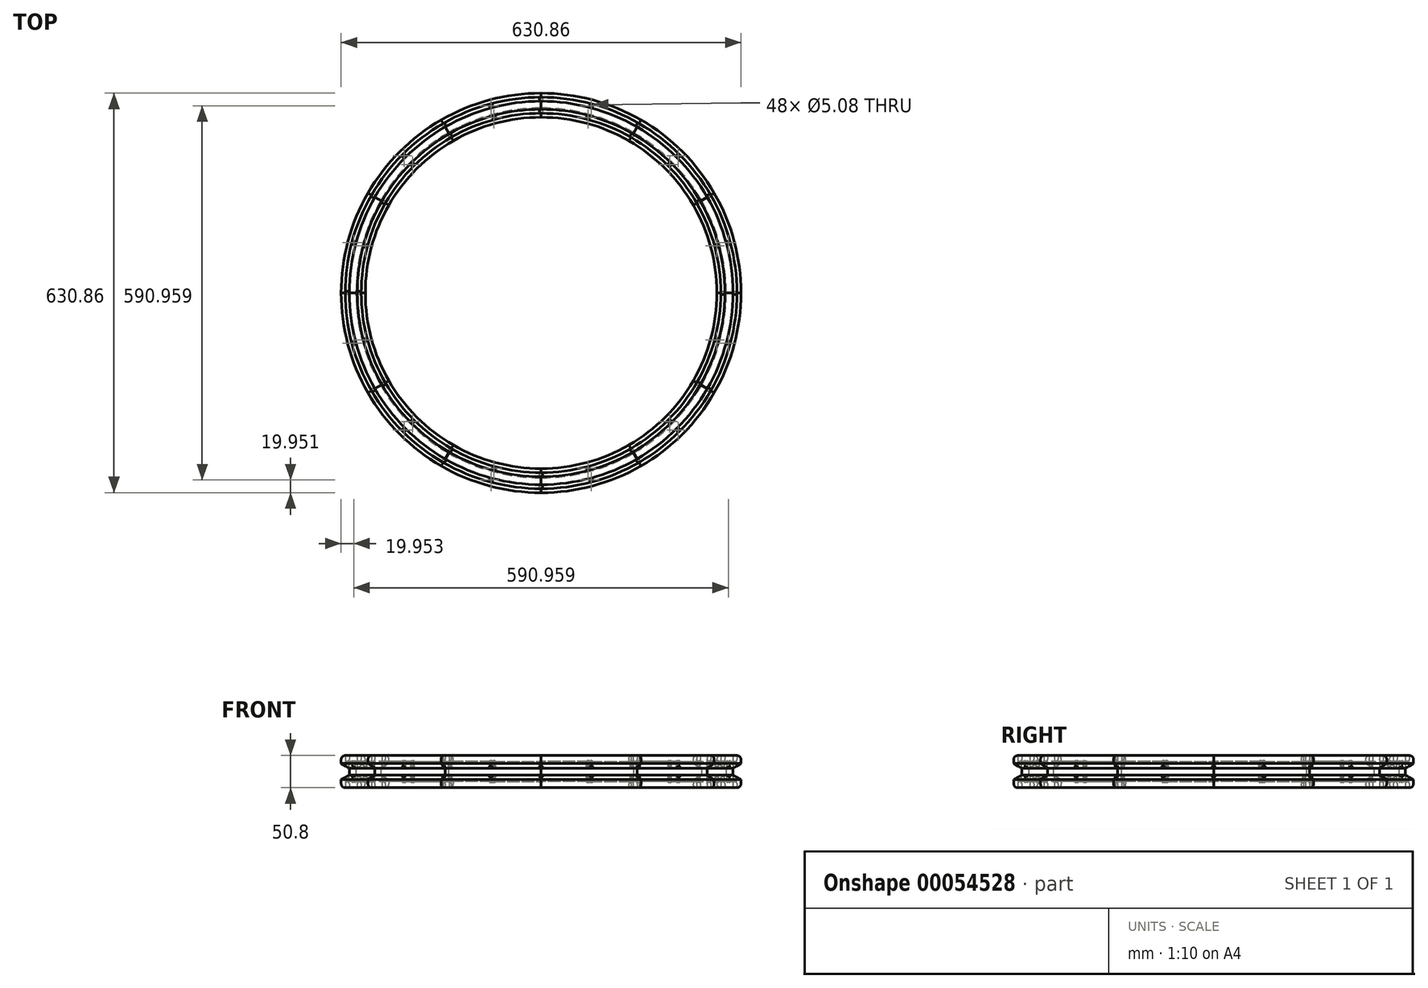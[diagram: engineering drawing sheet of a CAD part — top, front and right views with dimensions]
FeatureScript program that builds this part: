
annotation { "Feature Type Name" : "Feature", "Feature Type Description" : "" }
export const myFeature = defineFeature(function(context is Context, id is Id, definition is map)
    precondition{}
    {
        {
            var Q0;
            Q0=qCreatedBy(makeId("Front.planeOp"),FACE);
            var sketch = newSketch(context, id + "F0", { "sketchPlane" : qUnion([Q0])});
            skLineSegment(sketch, "E0", {"start": v(-51.22, 16.91) * mm, "end": v(-51.22, 6.28) * mm});
            skPoint(sketch, "E1.visualSharp", {"position": v(-4.7, -13.74) * mm});
            skArc(sketch, "E1.filletArc", {"start": v(-42.8, -13.8) * mm, "mid": v(-38.3, -11.94) * mm, "end": v(-36.45, -7.45) * mm});
            skPoint(sketch, "E2.visualSharp", {"position": v(-4.7, 37.06) * mm});
            skArc(sketch, "E2.filletArc", {"start": v(-36.45, 30.65) * mm, "mid": v(-38.3, 35.14) * mm, "end": v(-42.8, 37) * mm});
            skPoint(sketch, "E3", {"position": v(240.88, 11.6) * mm});
            skLineSegment(sketch, "E4", {"start": v(240.88, 11.6) * mm, "end": v(240.88, 0) * mm});
            skLineSegment(sketch, "E5", {"start": v(-36.45, 24.3) * mm, "end": v(-51.22, 16.91) * mm});
            skLineSegment(sketch, "E6", {"start": v(-36.45, 24.3) * mm, "end": v(-36.45, 30.65) * mm});
            skLineSegment(sketch, "E7", {"start": v(-36.45, -1.1) * mm, "end": v(-51.22, 6.28) * mm});
            skLineSegment(sketch, "E8", {"start": v(-36.45, -1.1) * mm, "end": v(-36.45, -7.45) * mm});
            skLineSegment(sketch, "E9", {"start": v(-51.22, 16.91) * mm, "end": v(-51.22, 11.6) * mm});
            skLineSegment(sketch, "E10", {"start": v(-42.8, 303.76) * mm, "end": v(-52.22, 303.76) * mm});
            skPoint(sketch, "E11", {"position": v(-45.97, 30.7) * mm});
            skPoint(sketch, "E12", {"position": v(-45.97, -7.45) * mm});
            skPoint(sketch, "E13", {"position": v(-45.9, 27.47) * mm});
            skPoint(sketch, "E14", {"position": v(-49.15, 30.65) * mm});
            skPoint(sketch, "E15", {"position": v(-49.15, -7.45) * mm});
            skPoint(sketch, "E16", {"position": v(-45.97, -4.28) * mm});
            skArc(sketch, "E17", {"start": v(-42.8, -7.45) * mm, "mid": v(-45.97, -4.28) * mm, "end": v(-49.15, -7.45) * mm});
            skArc(sketch, "E18", {"start": v(-49.15, 30.65) * mm, "mid": v(-45.97, 27.47) * mm, "end": v(-42.8, 30.65) * mm});
            skLineSegment(sketch, "E19", {"start": v(-49.15, 37) * mm, "end": v(-49.15, 30.65) * mm});
            skLineSegment(sketch, "E20", {"start": v(-42.8, 37) * mm, "end": v(-42.8, 30.65) * mm});
            skLineSegment(sketch, "E21", {"start": v(-49.15, -7.45) * mm, "end": v(-49.15, -13.8) * mm});
            skLineSegment(sketch, "E22", {"start": v(-42.8, -7.45) * mm, "end": v(-42.8, -13.8) * mm});
            skLineSegment(sketch, "E23", {"start": v(-49.15, 37) * mm, "end": v(-61.85, 37) * mm});
            skLineSegment(sketch, "E24", {"start": v(-49.15, -13.8) * mm, "end": v(-61.85, -13.8) * mm});
            skLineSegment(sketch, "E25", {"start": v(-36.45, 16.91) * mm, "end": v(-36.45, 24.3) * mm, "construction": true});
            skLineSegment(sketch, "E26", {"start": v(-36.45, 16.91) * mm, "end": v(-51.22, 16.91) * mm, "construction": true});
            skLineSegment(sketch, "E27", {"start": v(-36.45, 6.28) * mm, "end": v(-36.45, -1.1) * mm, "construction": true});
            skLineSegment(sketch, "E28", {"start": v(-36.45, 6.28) * mm, "end": v(-51.22, 6.28) * mm, "construction": true});
            skPoint(sketch, "E29", {"position": v(-61.85, -7.45) * mm});
            skLineSegment(sketch, "E30", {"start": v(-61.85, -13.8) * mm, "end": v(-68.2, -13.8) * mm, "construction": true});
            skLineSegment(sketch, "E31", {"start": v(-68.2, -7.45) * mm, "end": v(-68.2, -13.8) * mm});
            skPoint(sketch, "E32", {"position": v(-65.02, -4.28) * mm});
            skPoint(sketch, "E32.positionSnap0", {"position": v(-65.02, -13.8) * mm});
            skArc(sketch, "E33", {"start": v(-61.85, -7.45) * mm, "mid": v(-65.02, -4.28) * mm, "end": v(-68.2, -7.45) * mm});
            skLineSegment(sketch, "E34", {"start": v(-68.2, -13.8) * mm, "end": v(-68.2, -13.8) * mm});
            skLineSegment(sketch, "E35", {"start": v(-74.55, -7.45) * mm, "end": v(-74.55, -7.45) * mm});
            skPoint(sketch, "E36.visualSharp", {"position": v(-74.55, -13.8) * mm});
            skArc(sketch, "E36.filletArc", {"start": v(-74.55, -7.45) * mm, "mid": v(-72.69, -11.94) * mm, "end": v(-68.2, -13.8) * mm});
            skLineSegment(sketch, "E37", {"start": v(-74.55, 30.65) * mm, "end": v(-74.55, -7.45) * mm, "construction": true});
            skLineSegment(sketch, "E38", {"start": v(-74.55, -7.45) * mm, "end": v(-74.55, -1.1) * mm});
            skLineSegment(sketch, "E39", {"start": v(-74.55, -1.1) * mm, "end": v(-61.85, 6.28) * mm});
            skLineSegment(sketch, "E40", {"start": v(-61.85, 16.91) * mm, "end": v(-74.55, 24.3) * mm});
            skLineSegment(sketch, "E41", {"start": v(-61.85, -7.45) * mm, "end": v(-61.85, -13.8) * mm});
            skLineSegment(sketch, "E42", {"start": v(-61.85, 6.28) * mm, "end": v(-61.85, 16.91) * mm});
            skLineSegment(sketch, "E43", {"start": v(-74.55, 24.3) * mm, "end": v(-74.55, 30.65) * mm});
            skLineSegment(sketch, "E44", {"start": v(-74.55, 30.65) * mm, "end": v(-74.55, 30.65) * mm});
            skLineSegment(sketch, "E45", {"start": v(-68.2, 37) * mm, "end": v(-68.2, 37) * mm});
            skPoint(sketch, "E45.endSnap0", {"position": v(-68.2, 20.6) * mm});
            skLineSegment(sketch, "E46", {"start": v(-68.2, 37) * mm, "end": v(-61.85, 37) * mm, "construction": true});
            skPoint(sketch, "E47.visualSharp", {"position": v(-74.55, 37) * mm});
            skArc(sketch, "E47.filletArc", {"start": v(-68.2, 37) * mm, "mid": v(-72.69, 35.14) * mm, "end": v(-74.55, 30.65) * mm});
            skLineSegment(sketch, "E48", {"start": v(-68.2, 37) * mm, "end": v(-68.2, 30.65) * mm});
            skLineSegment(sketch, "E49", {"start": v(-61.85, 37) * mm, "end": v(-61.85, 30.65) * mm});
            skPoint(sketch, "E50", {"position": v(-65.02, 27.47) * mm});
            skArc(sketch, "E51", {"start": v(-68.2, 30.65) * mm, "mid": v(-65.02, 27.47) * mm, "end": v(-61.85, 30.65) * mm});
            skSolve(sketch);
        }
        {
            var Q0;
            Q0=makeQuery(id+"F0.imprint","IMPRINT",FACE,{"disambiguationData":[TD([[makeQuery(id+"F0.imprint","IMPRINT",EDGE,{"derivedFrom":sQuery(id+"F0.wireOp",EDGE,"E0")}),-1.0]])]});
            var Q1;
            Q1=sQuery(id+"F0.wireOp",EDGE,"E4");
            revolve(context, id + "F1", {"entities" : qUnion([Q0]), "axis" : qUnion([Q1]), "revolveType" : RevolveType.ONE_DIRECTION, "angle" : 30 * degree});
        }
        {
            var Q0;
            Q0=makeQuery(id+"F1.opRevolve","SWEPT_FACE",FACE,{"disambiguationData":[OSD([sQuery(id+"F0.wireOp",EDGE,"E23")])]});
            var sketch = newSketch(context, id + "F2", { "sketchPlane" : qUnion([Q0])});
            skPoint(sketch, "E52", {"position": v(-61.85, 0) * mm});
            skPoint(sketch, "E53", {"position": v(-49.15, 0) * mm});
            skLineSegment(sketch, "E54", {"start": v(-61.85, 0) * mm, "end": v(-68.2, 0) * mm});
            skPoint(sketch, "E55", {"position": v(-65.02, 0) * mm});
            skPoint(sketch, "E56", {"position": v(-68.2, 0) * mm});
            skPoint(sketch, "E57", {"position": v(-21.29, 151.36) * mm});
            skLineSegment(sketch, "E58", {"start": v(-21.29, 151.36) * mm, "end": v(-26.79, 154.54) * mm});
            skPoint(sketch, "E59", {"position": v(-24.04, 152.95) * mm});
            skPoint(sketch, "E60", {"position": v(-51.53, 78.35) * mm});
            skArc(sketch, "E61", {"start": v(-68.2, 0) * mm, "mid": v(-57.66, 80) * mm, "end": v(-26.79, 154.54) * mm});
            skPoint(sketch, "E62", {"position": v(-57.66, 80) * mm});
            skLineSegment(sketch, "E63", {"start": v(-51.53, 78.35) * mm, "end": v(-57.66, 80) * mm});
            skPoint(sketch, "E64", {"position": v(-54.6, 79.17) * mm});
            skPoint(sketch, "E65", {"position": v(-10.29, 145.01) * mm});
            skPoint(sketch, "E66", {"position": v(-39.26, 75.06) * mm});
            skArc(sketch, "E67", {"start": v(-49.15, 0) * mm, "mid": v(-39.26, 75.06) * mm, "end": v(-10.29, 145.01) * mm});
            skLineSegment(sketch, "E68", {"start": v(-49.15, 0) * mm, "end": v(-42.8, 0) * mm});
            skPoint(sketch, "E69", {"position": v(-42.8, 0) * mm});
            skLineSegment(sketch, "E70", {"start": v(-10.29, 145.01) * mm, "end": v(-4.79, 141.84) * mm});
            skPoint(sketch, "E71", {"position": v(-4.79, 141.84) * mm});
            skArc(sketch, "E72", {"start": v(-42.8, 0) * mm, "mid": v(-33.13, 73.42) * mm, "end": v(-4.79, 141.84) * mm});
            skPoint(sketch, "E73", {"position": v(-33.13, 73.42) * mm});
            skLineSegment(sketch, "E74", {"start": v(-39.26, 75.06) * mm, "end": v(-33.13, 73.42) * mm});
            skPoint(sketch, "E75", {"position": v(-36.2, 73.42) * mm});
            skPoint(sketch, "E75.positionSnap0", {"position": v(-36.2, 74.24) * mm});
            skPoint(sketch, "E76", {"position": v(-45.97, 0) * mm});
            skPoint(sketch, "E77", {"position": v(-7.54, 143.43) * mm});
            skSolve(sketch);
        }
        {
            var Q0;
            Q0=sQuery(id+"F2.wireOp",VERTEX,"E64");
            var Q1;
            Q1=makeQuery(id+"F1.opRevolve","SWEPT_BODY",BODY,{"disambiguationData":[OSD([sQuery(id+"F0.wireOp",EDGE,"E0"),sQuery(id+"F0.wireOp",EDGE,"E1.filletArc"),sQuery(id+"F0.wireOp",EDGE,"E2.filletArc"),sQuery(id+"F0.wireOp",EDGE,"E5"),sQuery(id+"F0.wireOp",EDGE,"E6"),sQuery(id+"F0.wireOp",EDGE,"E7"),sQuery(id+"F0.wireOp",EDGE,"E8"),sQuery(id+"F0.wireOp",EDGE,"E9"),sQuery(id+"F0.wireOp",EDGE,"E17"),sQuery(id+"F0.wireOp",EDGE,"E18"),sQuery(id+"F0.wireOp",EDGE,"E19"),sQuery(id+"F0.wireOp",EDGE,"E20"),sQuery(id+"F0.wireOp",EDGE,"E21"),sQuery(id+"F0.wireOp",EDGE,"E22"),sQuery(id+"F0.wireOp",EDGE,"E23"),sQuery(id+"F0.wireOp",EDGE,"E24"),sQuery(id+"F0.wireOp",EDGE,"E31"),sQuery(id+"F0.wireOp",EDGE,"E33"),sQuery(id+"F0.wireOp",EDGE,"E36.filletArc"),sQuery(id+"F0.wireOp",EDGE,"E38"),sQuery(id+"F0.wireOp",EDGE,"E39"),sQuery(id+"F0.wireOp",EDGE,"E40"),sQuery(id+"F0.wireOp",EDGE,"E41"),sQuery(id+"F0.wireOp",EDGE,"E42"),sQuery(id+"F0.wireOp",EDGE,"E43"),sQuery(id+"F0.wireOp",EDGE,"E47.filletArc"),sQuery(id+"F0.wireOp",EDGE,"E48"),sQuery(id+"F0.wireOp",EDGE,"E49"),sQuery(id+"F0.wireOp",EDGE,"E51")])]});
            hole(context, id + "F3", {"style" : HoleStyle.SIMPLE, "endStyle" : HoleEndStyle.THROUGH, "holeDiameter" : 5.08 * mm, "locations" : qUnion([Q0]), "scope" : qUnion([Q1]), "isTappedThrough" : true});
        }
        {
            var Q0;
            Q0=sQuery(id+"F2.wireOp",VERTEX,"E55");
            var Q1;
            Q1=makeQuery(id+"F1.opRevolve","SWEPT_BODY",BODY,{"disambiguationData":[OSD([sQuery(id+"F0.wireOp",EDGE,"E0"),sQuery(id+"F0.wireOp",EDGE,"E1.filletArc"),sQuery(id+"F0.wireOp",EDGE,"E2.filletArc"),sQuery(id+"F0.wireOp",EDGE,"E5"),sQuery(id+"F0.wireOp",EDGE,"E6"),sQuery(id+"F0.wireOp",EDGE,"E7"),sQuery(id+"F0.wireOp",EDGE,"E8"),sQuery(id+"F0.wireOp",EDGE,"E9"),sQuery(id+"F0.wireOp",EDGE,"E17"),sQuery(id+"F0.wireOp",EDGE,"E18"),sQuery(id+"F0.wireOp",EDGE,"E19"),sQuery(id+"F0.wireOp",EDGE,"E20"),sQuery(id+"F0.wireOp",EDGE,"E21"),sQuery(id+"F0.wireOp",EDGE,"E22"),sQuery(id+"F0.wireOp",EDGE,"E23"),sQuery(id+"F0.wireOp",EDGE,"E24"),sQuery(id+"F0.wireOp",EDGE,"E31"),sQuery(id+"F0.wireOp",EDGE,"E33"),sQuery(id+"F0.wireOp",EDGE,"E36.filletArc"),sQuery(id+"F0.wireOp",EDGE,"E38"),sQuery(id+"F0.wireOp",EDGE,"E39"),sQuery(id+"F0.wireOp",EDGE,"E40"),sQuery(id+"F0.wireOp",EDGE,"E41"),sQuery(id+"F0.wireOp",EDGE,"E42"),sQuery(id+"F0.wireOp",EDGE,"E43"),sQuery(id+"F0.wireOp",EDGE,"E47.filletArc"),sQuery(id+"F0.wireOp",EDGE,"E48"),sQuery(id+"F0.wireOp",EDGE,"E49"),sQuery(id+"F0.wireOp",EDGE,"E51")])]});
            hole(context, id + "F4", {"style" : HoleStyle.SIMPLE, "endStyle" : HoleEndStyle.THROUGH, "holeDiameter" : 5.08 * mm, "locations" : qUnion([Q0]), "scope" : qUnion([Q1]), "isTappedThrough" : true});
        }
        {
            var Q0;
            Q0=sQuery(id+"F2.wireOp",VERTEX,"E59");
            var Q1;
            Q1=makeQuery(id+"F1.opRevolve","SWEPT_BODY",BODY,{"disambiguationData":[OSD([sQuery(id+"F0.wireOp",EDGE,"E0"),sQuery(id+"F0.wireOp",EDGE,"E1.filletArc"),sQuery(id+"F0.wireOp",EDGE,"E2.filletArc"),sQuery(id+"F0.wireOp",EDGE,"E5"),sQuery(id+"F0.wireOp",EDGE,"E6"),sQuery(id+"F0.wireOp",EDGE,"E7"),sQuery(id+"F0.wireOp",EDGE,"E8"),sQuery(id+"F0.wireOp",EDGE,"E9"),sQuery(id+"F0.wireOp",EDGE,"E17"),sQuery(id+"F0.wireOp",EDGE,"E18"),sQuery(id+"F0.wireOp",EDGE,"E19"),sQuery(id+"F0.wireOp",EDGE,"E20"),sQuery(id+"F0.wireOp",EDGE,"E21"),sQuery(id+"F0.wireOp",EDGE,"E22"),sQuery(id+"F0.wireOp",EDGE,"E23"),sQuery(id+"F0.wireOp",EDGE,"E24"),sQuery(id+"F0.wireOp",EDGE,"E31"),sQuery(id+"F0.wireOp",EDGE,"E33"),sQuery(id+"F0.wireOp",EDGE,"E36.filletArc"),sQuery(id+"F0.wireOp",EDGE,"E38"),sQuery(id+"F0.wireOp",EDGE,"E39"),sQuery(id+"F0.wireOp",EDGE,"E40"),sQuery(id+"F0.wireOp",EDGE,"E41"),sQuery(id+"F0.wireOp",EDGE,"E42"),sQuery(id+"F0.wireOp",EDGE,"E43"),sQuery(id+"F0.wireOp",EDGE,"E47.filletArc"),sQuery(id+"F0.wireOp",EDGE,"E48"),sQuery(id+"F0.wireOp",EDGE,"E49"),sQuery(id+"F0.wireOp",EDGE,"E51")])]});
            hole(context, id + "F5", {"style" : HoleStyle.SIMPLE, "endStyle" : HoleEndStyle.THROUGH, "holeDiameter" : 5.08 * mm, "locations" : qUnion([Q0]), "scope" : qUnion([Q1]), "isTappedThrough" : true});
        }
        {
            var Q0;
            Q0=sQuery(id+"F2.wireOp",VERTEX,"E76");
            var Q1;
            Q1=makeQuery(id+"F1.opRevolve","SWEPT_BODY",BODY,{"disambiguationData":[OSD([sQuery(id+"F0.wireOp",EDGE,"E0"),sQuery(id+"F0.wireOp",EDGE,"E1.filletArc"),sQuery(id+"F0.wireOp",EDGE,"E2.filletArc"),sQuery(id+"F0.wireOp",EDGE,"E5"),sQuery(id+"F0.wireOp",EDGE,"E6"),sQuery(id+"F0.wireOp",EDGE,"E7"),sQuery(id+"F0.wireOp",EDGE,"E8"),sQuery(id+"F0.wireOp",EDGE,"E9"),sQuery(id+"F0.wireOp",EDGE,"E17"),sQuery(id+"F0.wireOp",EDGE,"E18"),sQuery(id+"F0.wireOp",EDGE,"E19"),sQuery(id+"F0.wireOp",EDGE,"E20"),sQuery(id+"F0.wireOp",EDGE,"E21"),sQuery(id+"F0.wireOp",EDGE,"E22"),sQuery(id+"F0.wireOp",EDGE,"E23"),sQuery(id+"F0.wireOp",EDGE,"E24"),sQuery(id+"F0.wireOp",EDGE,"E31"),sQuery(id+"F0.wireOp",EDGE,"E33"),sQuery(id+"F0.wireOp",EDGE,"E36.filletArc"),sQuery(id+"F0.wireOp",EDGE,"E38"),sQuery(id+"F0.wireOp",EDGE,"E39"),sQuery(id+"F0.wireOp",EDGE,"E40"),sQuery(id+"F0.wireOp",EDGE,"E41"),sQuery(id+"F0.wireOp",EDGE,"E42"),sQuery(id+"F0.wireOp",EDGE,"E43"),sQuery(id+"F0.wireOp",EDGE,"E47.filletArc"),sQuery(id+"F0.wireOp",EDGE,"E48"),sQuery(id+"F0.wireOp",EDGE,"E49"),sQuery(id+"F0.wireOp",EDGE,"E51")])]});
            hole(context, id + "F6", {"style" : HoleStyle.SIMPLE, "endStyle" : HoleEndStyle.THROUGH, "holeDiameter" : 5.08 * mm, "locations" : qUnion([Q0]), "scope" : qUnion([Q1]), "isTappedThrough" : true});
        }
        {
            var Q0;
            Q0=sQuery(id+"F2.wireOp",VERTEX,"E75.positionSnap0");
            var Q1;
            Q1=makeQuery(id+"F1.opRevolve","SWEPT_BODY",BODY,{"disambiguationData":[OSD([sQuery(id+"F0.wireOp",EDGE,"E0"),sQuery(id+"F0.wireOp",EDGE,"E1.filletArc"),sQuery(id+"F0.wireOp",EDGE,"E2.filletArc"),sQuery(id+"F0.wireOp",EDGE,"E5"),sQuery(id+"F0.wireOp",EDGE,"E6"),sQuery(id+"F0.wireOp",EDGE,"E7"),sQuery(id+"F0.wireOp",EDGE,"E8"),sQuery(id+"F0.wireOp",EDGE,"E9"),sQuery(id+"F0.wireOp",EDGE,"E17"),sQuery(id+"F0.wireOp",EDGE,"E18"),sQuery(id+"F0.wireOp",EDGE,"E19"),sQuery(id+"F0.wireOp",EDGE,"E20"),sQuery(id+"F0.wireOp",EDGE,"E21"),sQuery(id+"F0.wireOp",EDGE,"E22"),sQuery(id+"F0.wireOp",EDGE,"E23"),sQuery(id+"F0.wireOp",EDGE,"E24"),sQuery(id+"F0.wireOp",EDGE,"E31"),sQuery(id+"F0.wireOp",EDGE,"E33"),sQuery(id+"F0.wireOp",EDGE,"E36.filletArc"),sQuery(id+"F0.wireOp",EDGE,"E38"),sQuery(id+"F0.wireOp",EDGE,"E39"),sQuery(id+"F0.wireOp",EDGE,"E40"),sQuery(id+"F0.wireOp",EDGE,"E41"),sQuery(id+"F0.wireOp",EDGE,"E42"),sQuery(id+"F0.wireOp",EDGE,"E43"),sQuery(id+"F0.wireOp",EDGE,"E47.filletArc"),sQuery(id+"F0.wireOp",EDGE,"E48"),sQuery(id+"F0.wireOp",EDGE,"E49"),sQuery(id+"F0.wireOp",EDGE,"E51")])]});
            hole(context, id + "F7", {"style" : HoleStyle.SIMPLE, "endStyle" : HoleEndStyle.THROUGH, "holeDiameter" : 5.08 * mm, "locations" : qUnion([Q0]), "scope" : qUnion([Q1]), "isTappedThrough" : true});
        }
        {
            var Q0;
            Q0=sQuery(id+"F2.wireOp",VERTEX,"E77");
            var Q1;
            Q1=makeQuery(id+"F1.opRevolve","SWEPT_BODY",BODY,{"disambiguationData":[OSD([sQuery(id+"F0.wireOp",EDGE,"E0"),sQuery(id+"F0.wireOp",EDGE,"E1.filletArc"),sQuery(id+"F0.wireOp",EDGE,"E2.filletArc"),sQuery(id+"F0.wireOp",EDGE,"E5"),sQuery(id+"F0.wireOp",EDGE,"E6"),sQuery(id+"F0.wireOp",EDGE,"E7"),sQuery(id+"F0.wireOp",EDGE,"E8"),sQuery(id+"F0.wireOp",EDGE,"E9"),sQuery(id+"F0.wireOp",EDGE,"E17"),sQuery(id+"F0.wireOp",EDGE,"E18"),sQuery(id+"F0.wireOp",EDGE,"E19"),sQuery(id+"F0.wireOp",EDGE,"E20"),sQuery(id+"F0.wireOp",EDGE,"E21"),sQuery(id+"F0.wireOp",EDGE,"E22"),sQuery(id+"F0.wireOp",EDGE,"E23"),sQuery(id+"F0.wireOp",EDGE,"E24"),sQuery(id+"F0.wireOp",EDGE,"E31"),sQuery(id+"F0.wireOp",EDGE,"E33"),sQuery(id+"F0.wireOp",EDGE,"E36.filletArc"),sQuery(id+"F0.wireOp",EDGE,"E38"),sQuery(id+"F0.wireOp",EDGE,"E39"),sQuery(id+"F0.wireOp",EDGE,"E40"),sQuery(id+"F0.wireOp",EDGE,"E41"),sQuery(id+"F0.wireOp",EDGE,"E42"),sQuery(id+"F0.wireOp",EDGE,"E43"),sQuery(id+"F0.wireOp",EDGE,"E47.filletArc"),sQuery(id+"F0.wireOp",EDGE,"E48"),sQuery(id+"F0.wireOp",EDGE,"E49"),sQuery(id+"F0.wireOp",EDGE,"E51")])]});
            hole(context, id + "F8", {"style" : HoleStyle.SIMPLE, "endStyle" : HoleEndStyle.THROUGH, "holeDiameter" : 5.08 * mm, "locations" : qUnion([Q0]), "scope" : qUnion([Q1]), "isTappedThrough" : true});
        }
        {
            var Q0;
            Q0=makeQuery(id+"F1.opRevolve","SWEPT_BODY",BODY,{"disambiguationData":[OSD([sQuery(id+"F0.wireOp",EDGE,"E0"),sQuery(id+"F0.wireOp",EDGE,"E1.filletArc"),sQuery(id+"F0.wireOp",EDGE,"E2.filletArc"),sQuery(id+"F0.wireOp",EDGE,"E5"),sQuery(id+"F0.wireOp",EDGE,"E6"),sQuery(id+"F0.wireOp",EDGE,"E7"),sQuery(id+"F0.wireOp",EDGE,"E8"),sQuery(id+"F0.wireOp",EDGE,"E9"),sQuery(id+"F0.wireOp",EDGE,"E17"),sQuery(id+"F0.wireOp",EDGE,"E18"),sQuery(id+"F0.wireOp",EDGE,"E19"),sQuery(id+"F0.wireOp",EDGE,"E20"),sQuery(id+"F0.wireOp",EDGE,"E21"),sQuery(id+"F0.wireOp",EDGE,"E22"),sQuery(id+"F0.wireOp",EDGE,"E23"),sQuery(id+"F0.wireOp",EDGE,"E24"),sQuery(id+"F0.wireOp",EDGE,"E31"),sQuery(id+"F0.wireOp",EDGE,"E33"),sQuery(id+"F0.wireOp",EDGE,"E36.filletArc"),sQuery(id+"F0.wireOp",EDGE,"E38"),sQuery(id+"F0.wireOp",EDGE,"E39"),sQuery(id+"F0.wireOp",EDGE,"E40"),sQuery(id+"F0.wireOp",EDGE,"E41"),sQuery(id+"F0.wireOp",EDGE,"E42"),sQuery(id+"F0.wireOp",EDGE,"E43"),sQuery(id+"F0.wireOp",EDGE,"E47.filletArc"),sQuery(id+"F0.wireOp",EDGE,"E48"),sQuery(id+"F0.wireOp",EDGE,"E49"),sQuery(id+"F0.wireOp",EDGE,"E51")])]});
            var Q1;
            Q1=sQuery(id+"F0.wireOp",EDGE,"E4");
            circularPattern(context, id + "F9", {"entities" : qUnion([Q0]), "axis" : qUnion([Q1]), "angle" : 360 * degree, "instanceCount" : 12, "equalSpace" : true});
        }
    });
